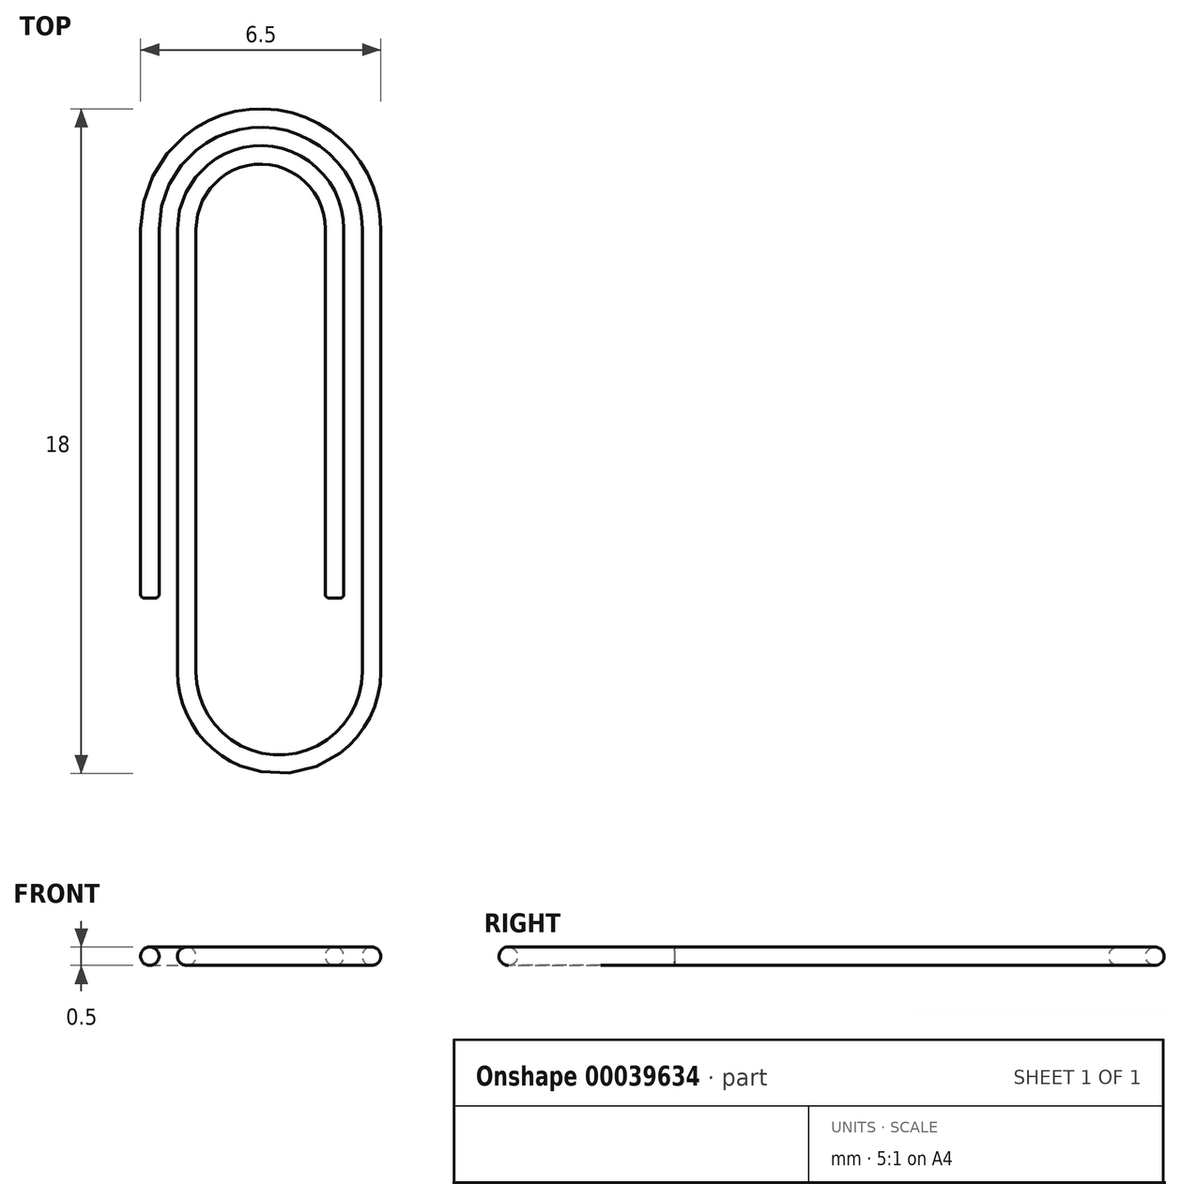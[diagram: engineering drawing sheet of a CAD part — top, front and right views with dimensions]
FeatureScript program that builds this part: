
annotation { "Feature Type Name" : "Feature", "Feature Type Description" : "" }
export const myFeature = defineFeature(function(context is Context, id is Id, definition is map)
    precondition{}
    {
        {
            var Q0;
            Q0=qCreatedBy(makeId("Top.planeOp"),FACE);
            var sketch = newSketch(context, id + "F0", { "sketchPlane" : qUnion([Q0])});
            skLineSegment(sketch, "E0", {"start": v(-3, 0) * mm, "end": v(-3, 10) * mm});
            skLineSegment(sketch, "E1", {"start": v(3, 10) * mm, "end": v(3, -2) * mm});
            skLineSegment(sketch, "E2", {"start": v(-2, -2) * mm, "end": v(-2, 10) * mm});
            skLineSegment(sketch, "E3", {"start": v(2, 10) * mm, "end": v(2, 0) * mm});
            skArc(sketch, "E4", {"start": v(-3, 10) * mm, "mid": v(0, 13) * mm, "end": v(3, 10) * mm});
            skArc(sketch, "E5", {"start": v(-2, 10) * mm, "mid": v(0, 12) * mm, "end": v(2, 10) * mm});
            skArc(sketch, "E6", {"start": v(3, -2) * mm, "mid": v(0.5, -4.5) * mm, "end": v(-2, -2) * mm});
            skSolve(sketch);
        }
        {
            var Q0;
            Q0=qCreatedBy(makeId("Front.planeOp"),FACE);
            var sketch = newSketch(context, id + "F1", { "sketchPlane" : qUnion([Q0])});
            skCircle(sketch, "E7", {"center": v(-3, 0) * mm, "radius": 0.25 * mm});
            skSolve(sketch);
        }
        {
            var Q0;
            Q0 = qSketchRegion(id + "F1", true);
            var Q1;
            Q1 = qConstructionFilter(qBodyType(qCreatedBy(id + "F0" ,EDGE), BodyType.WIRE), ConstructionObject.NO);
            sweep(context, id + "F2", {"profiles" : qUnion([Q0]), "path" : qUnion([Q1])});
        }
        {
            var Q0;
            Q0=makeQuery(id+"F2.opSweep","CAP_FACE",FACE,{"disambiguationData":[OSD([sQuery(id+"F0.wireOp",VERTEX,"E3.end"),sQuery(id+"F1.wireOp",EDGE,"E7")])],"isStart":false});
            var Q1;
            Q1=makeQuery(id+"F2.opSweep","CAP_FACE",FACE,{"disambiguationData":[OSD([sQuery(id+"F0.wireOp",VERTEX,"E0.start"),sQuery(id+"F1.wireOp",EDGE,"E7")])],"isStart":true});
            fillet(context, id + "F3", {"entities" : qUnion([Q0, Q1]), "radius" : 0.1 * mm, "tangentPropagation" : true, "allowEdgeOverflow" : false});
        }
    });
